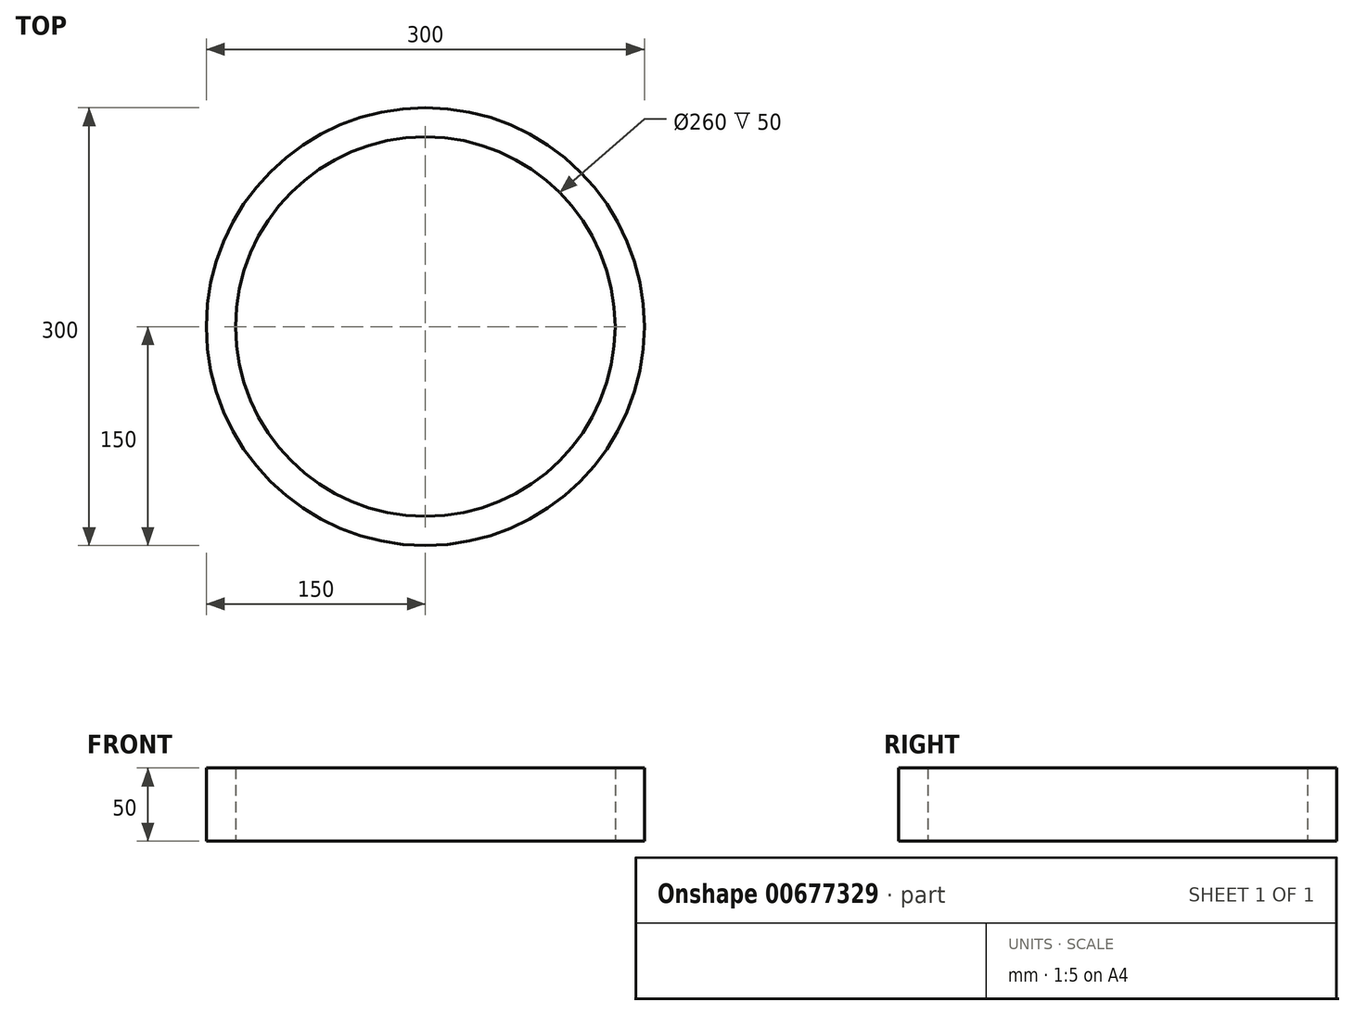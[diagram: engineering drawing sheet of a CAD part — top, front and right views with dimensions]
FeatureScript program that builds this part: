
annotation { "Feature Type Name" : "Feature", "Feature Type Description" : "" }
export const myFeature = defineFeature(function(context is Context, id is Id, definition is map)
    precondition{}
    {
        {
            var Q0;
            Q0=qCreatedBy(makeId("Top.planeOp"),FACE);
            var sketch = newSketch(context, id + "F0", { "sketchPlane" : qUnion([Q0])});
            skCircle(sketch, "E0", {"center": v(0, 0) * mm, "radius": 150 * mm});
            skCircle(sketch, "E1", {"center": v(0, 0) * mm, "radius": 130 * mm});
            skSolve(sketch);
        }
        {
            var Q0;
            Q0 = qSketchRegion(id + "F0", true);
            extrude(context, id + "F1", {"entities" : qUnion([Q0]), "depth" : 50 * mm, "offsetDistance" : 25 * mm});
        }
    });
